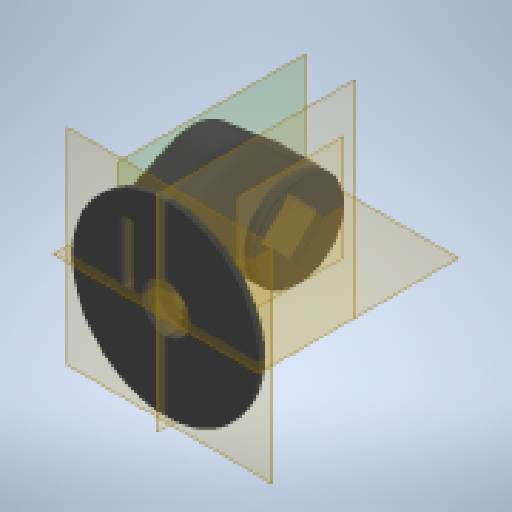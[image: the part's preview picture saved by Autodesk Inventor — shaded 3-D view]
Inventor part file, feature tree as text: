
AUTODESK INVENTOR PART (.ipt)
format: ipt  version: 2025.2 (Build 292293000, 293)  size: 479,744 bytes
history: native  units: mm
features: extrude x18, sketch x17, projected_geometry x6, fillet x5, plane x2, revolve x1, chamfer x1
ambient origin geometry x8: Origin, YZ Plane, XZ Plane, XY Plane, X Axis, Y Axis, Z Axis, Center Point
bodies: Solid2 (feature_tree)
feature tree (50):
  extrude  "Extrusion6"  Depth=5.0mm TaperAngle=0.0deg
  extrude  "Extrusion15"  Depth=35.0mm
  extrude  "Extrusion16"  Depth=8.1mm TaperAngle=0.0deg
  extrude  "Extrusion17"  Depth=3.0mm
  revolve  "Revolution2"  [1 undecoded]
  fillet  "Fillet8"  Radius=4.75mm
  extrude  "Extrusion18"  Depth=3.0mm
  plane  "Work Plane5"
  extrude  "Extrusion19"  Depth=65.0mm
  extrude  "Extrusion20"  [1 undecoded]
  extrude  "Extrusion21"  Depth=10.0mm TaperAngle=0.0deg
  extrude  "Extrusion22"  Depth=35.0mm
  extrude  "Extrusion23"  Depth=20.071286mm
  extrude  "Extrusion24"  Depth=10.0mm TaperAngle=0.0deg
  extrude  "Extrusion25"  Depth=15.0mm
  extrude  "Extrusion26"  Depth=10.0mm
  sketch  "Sketch30"  dims[d126=42.0mm d128=36.0mm]
  extrude  "Extrusion27"  Depth=36.0mm
  extrude  "Extrusion28"  Depth=15.0mm
  plane  "Work Plane6"
  extrude  "Extrusion29"  Depth=2.0mm
  fillet  "Fillet9"  Radius=21.0mm
  chamfer  "Chamfer2"  Distance=7.9mm
  fillet  "Fillet10"  Radius=11.0mm
  fillet  "Fillet11"  Radius=10.0mm
  sketch  "Sketch32"  dims[d132=12.5mm d133=0.0mm d135=41.0mm d136=21.0mm d137=7.9mm d138=11.0mm d139=10.0mm d140=0.0mm d141=14.253mm d142=0.0mm d143=0.0mm d144=10.0mm d145=2.6mm d146=3.5mm d147=4.0mm d148=8.5mm d149=4.0mm d150=0.0mm d151=7.5mm d152=0.0mm d153=-2.5mm d154=2.5mm d155=2.0mm d156=0.0mm d157=5.6mm d158=2.0mm d159=45.0deg d160=7.0mm d161=2.0mm d162=7.0mm d165=1.0mm d166=32.0mm d167=0.0mm d168=0.0mm d169=15.0mm d170=0.0mm d171=2.0mm d134=0.5mm]
  extrude  "Extrusion30"  Depth=2.0mm
  extrude  "Extrusion31"  TaperAngle=0.0deg  [1 undecoded]
  fillet  "Fillet12"  Radius=10.0mm
  sketch  "Sketch8"  dims[d28=98.0mm d30=5.0mm d31=0.0mm]
  sketch  "Sketch16"  dims[d90=5.6mm d91=0.0mm d92=35.0mm]
  sketch  "Sketch17"  dims[d93=25.0mm d94=8.1mm d95=0.0mm]
  sketch  "Sketch18"  dims[d96=7.0mm d97=3.0mm]
  sketch  "Sketch19"  dims[d98=14.5mm d99=8.1mm d100=0.0mm d101=4.75mm]
  sketch  "Sketch20"  dims[d102=90.0deg d103=3.0mm]
  sketch  "Sketch21"  dims[d104=50.0mm d105=65.0mm]
  sketch  "Sketch22"  dims[d106=28.5mm d107=0.0mm d108=-4.0mm]
  projected_geometry  "Projected Loop2"
  sketch  "Sketch23"  dims[d109=28.5mm d110=0.0mm d111=10.0mm d112=0.0mm]
  sketch  "Sketch25"  dims[d113=8.726646mm d114=35.0mm]
  projected_geometry  "Projected Loop3"
  sketch  "Sketch26"  dims[d115=25.0mm d116=20.071286mm]
  projected_geometry  "Projected Loop4"
  sketch  "Sketch27"  dims[d117=10.0mm d118=0.0mm d119=10.0mm d120=0.0mm]
  projected_geometry  "Projected Loop5"
  sketch  "Sketch28"  dims[d121=11.34464mm d122=15.0mm]
  projected_geometry  "Projected Loop6"
  sketch  "Sketch29"  dims[d123=10.0mm d124=0.0mm d125=41.0mm]
  projected_geometry  "Projected Loop7"
  sketch  "Sketch31"  dims[d129=17.0mm d131=15.0mm]
note: 3 required parameter values undecoded (feature->parameter linkage not recoverable at this tier; creation-order binding heuristic only, values carry confidence <= 0.55)